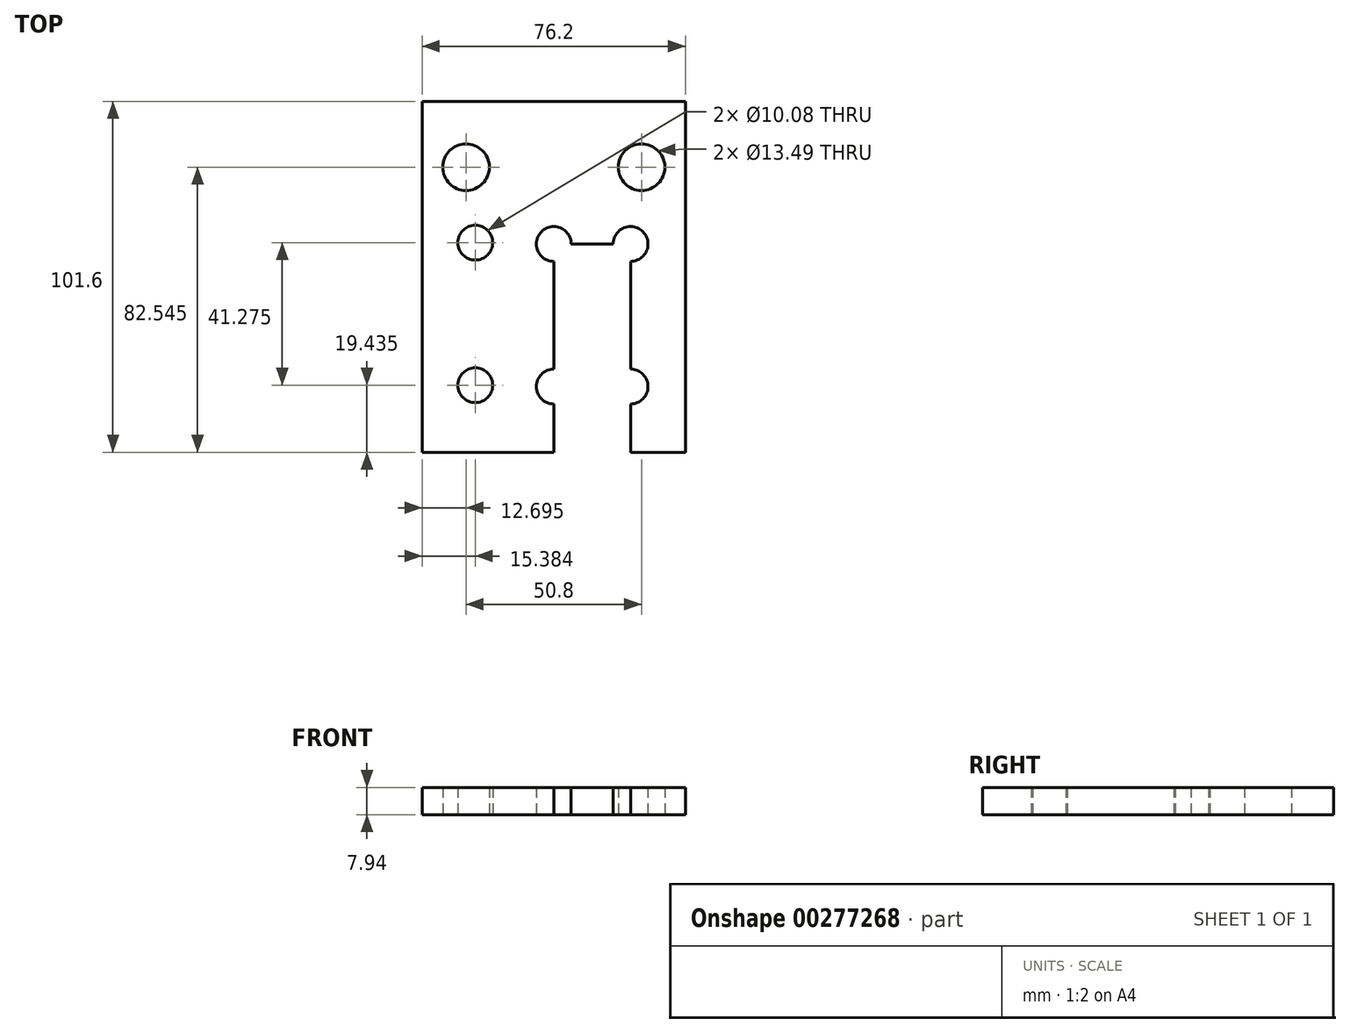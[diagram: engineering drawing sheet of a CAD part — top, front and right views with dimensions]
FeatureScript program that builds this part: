
annotation { "Feature Type Name" : "Feature", "Feature Type Description" : "" }
export const myFeature = defineFeature(function(context is Context, id is Id, definition is map)
    precondition{}
    {
        {
            var Q0;
            Q0=qCreatedBy(makeId("Top.planeOp"),FACE);
            var sketch = newSketch(context, id + "F0", { "sketchPlane" : qUnion([Q0])});
            skLineSegment(sketch, "E0.bottom", {"start": v(-37.95, 40.89) * mm, "end": v(38.25, 40.89) * mm});
            skLineSegment(sketch, "E0.top", {"start": v(-37.95, -60.71) * mm, "end": v(38.25, -60.71) * mm});
            skLineSegment(sketch, "E0.left", {"start": v(-37.95, 40.89) * mm, "end": v(-37.95, -60.71) * mm});
            skLineSegment(sketch, "E0.right", {"start": v(38.25, 40.89) * mm, "end": v(38.25, -60.71) * mm});
            skPoint(sketch, "E1", {"position": v(38.25, 40.89) * mm});
            skLineSegment(sketch, "E2", {"start": v(-25.25, 21.84) * mm, "end": v(-25.25, 40.89) * mm});
            skLineSegment(sketch, "E3", {"start": v(25.55, 21.84) * mm, "end": v(25.55, 40.89) * mm});
            skLineSegment(sketch, "E4", {"start": v(-25.25, 21.84) * mm, "end": v(-37.95, 21.84) * mm});
            skLineSegment(sketch, "E5", {"start": v(25.55, 21.84) * mm, "end": v(38.25, 21.84) * mm});
            skLineSegment(sketch, "E6", {"start": v(0.15, -0.39) * mm, "end": v(0.15, -41.66) * mm});
            skLineSegment(sketch, "E7", {"start": v(0.15, -41.66) * mm, "end": v(0.15, -60.71) * mm});
            skLineSegment(sketch, "E8", {"start": v(22.37, -0.39) * mm, "end": v(22.37, -41.66) * mm});
            skLineSegment(sketch, "E9", {"start": v(22.37, -41.66) * mm, "end": v(22.37, -60.71) * mm});
            skLineSegment(sketch, "E10", {"start": v(0.15, -0.39) * mm, "end": v(22.37, -0.39) * mm});
            skLineSegment(sketch, "E11", {"start": v(-22.57, 0) * mm, "end": v(-22.57, -41.28) * mm});
            skLineSegment(sketch, "E12", {"start": v(-22.57, -41.28) * mm, "end": v(-22.57, -60.33) * mm});
            skLineSegment(sketch, "E13", {"start": v(-22.57, 0) * mm, "end": v(-0.34, 0) * mm});
            skSolve(sketch);
        }
        {
            var Q0;
            {var subQ0=sQuery(id+"F0.wireOp",EDGE,"lcWCMHyC-eplE-XHto-Is1u-1jWQCE3xKe38");Q0=makeQuery(id+"F0.imprint","IMPRINT",FACE,{"disambiguationData":[TD([[makeQuery(id+"F0.imprint","IMPRINT",EDGE,{"derivedFrom":subQ0}),-1.0]])]});}
            var Q1;
            {var subQ0=sQuery(id+"F0.wireOp",EDGE,"PR7J1r9g-NyIZ-4EAv-97Ck-6R3T5vIXL9lI");Q1=makeQuery(id+"F0.imprint","IMPRINT",FACE,{"disambiguationData":[TD([[makeQuery(id+"F0.imprint","IMPRINT",EDGE,{"derivedFrom":subQ0}),-1.0]])]});}
            var Q2;
            {var subQ5=sQuery(id+"F0.wireOp",EDGE,"E0.top");Q2=makeQuery(id+"F0.imprint","IMPRINT",FACE,{"disambiguationData":[TD([[makeQuery(id+"F0.imprint","IMPRINT",EDGE,{"derivedFrom":subQ5}),1.0]])]});}
            var Q3;
            {var subQ3=sQuery(id+"F0.wireOp",EDGE,"0CVaf1VI-ZbOA-vU7j-4cAE-WN4LLiThvYsT");var subQ5=sQuery(id+"F0.wireOp",EDGE,"E0.left");var subQ6=makeQuery(id+"F0.imprint","INTERSECT",VERTEX,{"derivedFrom":[subQ3,subQ5]});Q3=makeQuery(id+"F0.imprint","IMPRINT",FACE,{"disambiguationData":[TD([[makeQuery(id+"F0.imprint","IMPRINT",EDGE,{"disambiguationData":[TD([[subQ6,-1.0]])],"derivedFrom":subQ3}),1.0]])]});}
            var Q4;
            {var subQ0=sQuery(id+"F0.wireOp",EDGE,"E2");var subQ1=sQuery(id+"F0.wireOp",EDGE,"LTa7V2wM-ZibM-cuZf-cZ65-yHtlyJLLMwwq");var subQ2=makeQuery(id+"F0.imprint","INTERSECT",VERTEX,{"derivedFrom":[subQ1,subQ0]});Q4=makeQuery(id+"F0.imprint","IMPRINT",FACE,{"disambiguationData":[TD([[makeQuery(id+"F0.imprint","IMPRINT",EDGE,{"disambiguationData":[TD([[subQ2,-1.0]])],"derivedFrom":subQ1}),-1.0]])]});}
            var Q5;
            {var subQ0=sQuery(id+"F0.wireOp",EDGE,"E3");var subQ1=sQuery(id+"F0.wireOp",EDGE,"ef0b0393-9919-4fb4-960b-99aeebce1d35");var subQ2=makeQuery(id+"F0.imprint","INTERSECT",VERTEX,{"derivedFrom":[subQ1,subQ0]});Q5=makeQuery(id+"F0.imprint","IMPRINT",FACE,{"disambiguationData":[TD([[makeQuery(id+"F0.imprint","IMPRINT",EDGE,{"disambiguationData":[TD([[subQ2,1.0]])],"derivedFrom":subQ1}),-1.0]])]});}
            var Q6;
            {var subQ0=sQuery(id+"F0.wireOp",EDGE,"leSzz3VN-8iKC-pAnP-wKXI-R4EXnybGQ6SQ");Q6=makeQuery(id+"F0.imprint","IMPRINT",FACE,{"disambiguationData":[TD([[makeQuery(id+"F0.imprint","IMPRINT",EDGE,{"derivedFrom":subQ0}),-1.0]])]});}
            var Q7;
            {var subQ0=sQuery(id+"F0.wireOp",EDGE,"sYbMa3EQ-lgzP-OEaw-l84T-zbEHqADuA0Jr");Q7=makeQuery(id+"F0.imprint","IMPRINT",FACE,{"disambiguationData":[TD([[makeQuery(id+"F0.imprint","IMPRINT",EDGE,{"derivedFrom":subQ0}),-1.0]])]});}
            var Q8;
            {var subQ7=sQuery(id+"F0.wireOp",EDGE,"2inGmozC-EzYw-nWrg-dNEA-qCZoMKFbgd93");Q8=makeQuery(id+"F0.imprint","IMPRINT",FACE,{"disambiguationData":[TD([[makeQuery(id+"F0.imprint","IMPRINT",EDGE,{"derivedFrom":subQ7}),-1.0]])]});}
            var Q9;
            {var subQ3=sQuery(id+"F0.wireOp",EDGE,"E2");Q9=makeQuery(id+"F0.imprint","IMPRINT",FACE,{"disambiguationData":[TD([[makeQuery(id+"F0.imprint","IMPRINT",EDGE,{"derivedFrom":subQ3}),1.0]])]});}
            var Q10;
            {var subQ3=sQuery(id+"F0.wireOp",EDGE,"E3");Q10=makeQuery(id+"F0.imprint","IMPRINT",FACE,{"disambiguationData":[TD([[makeQuery(id+"F0.imprint","IMPRINT",EDGE,{"derivedFrom":subQ3}),-1.0]])]});}
            var Q11;
            Q11=makeQuery(id+"F0.imprint","IMPRINT",FACE,{"disambiguationData":[TD([[makeQuery(id+"F0.imprint","IMPRINT",EDGE,{"derivedFrom":sQuery(id+"F0.wireOp",EDGE,"E6")}),-1.0]])]});
            extrude(context, id + "F1", {"entities" : qUnion([Q0, Q1, Q2, Q3, Q4, Q5, Q6, Q7, Q8, Q9, Q10, Q11]), "depth" : 7.94 * mm});
        }
        {
            var Q0;
            Q0=sQuery(id+"F0.wireOp",VERTEX,"slWlOJYp-KtXo-T63F-XDAo-gwFZsbOWbfFg.start");
            var Q1;
            Q1=sQuery(id+"F0.wireOp",VERTEX,"2inGmozC-EzYw-nWrg-dNEA-qCZoMKFbgd93.start");
            var Q2;
            Q2=sQuery(id+"F0.wireOp",VERTEX,"E6.start");
            var Q3;
            Q3=sQuery(id+"F0.wireOp",VERTEX,"E7.start");
            var Q4;
            Q4=sQuery(id+"F0.wireOp",VERTEX,"f259f9f2-1a3e-449f-ba45-59925c1e67a2.start");
            var Q5;
            Q5=sQuery(id+"F0.wireOp",VERTEX,"06f6825e-fbd1-4fb1-a750-9c05bcffc3f1.start");
            var Q6;
            Q6=sQuery(id+"F0.wireOp",VERTEX,"E11.start");
            var Q7;
            Q7=sQuery(id+"F0.wireOp",VERTEX,"E12.start");
            var Q8;
            Q8=sQuery(id+"F0.wireOp",VERTEX,"E9.start");
            var Q9;
            Q9=sQuery(id+"F0.wireOp",VERTEX,"E8.start");
            var Q10;
            Q10=makeQuery(id+"F1.opExtrude","SWEPT_BODY",BODY,{"disambiguationData":[OSD([sQuery(id+"F0.wireOp",EDGE,"MnHyicGj-JLrE-Ki9W-tNHr-ggfPMjACvSpb.bottom"),sQuery(id+"F0.wireOp",EDGE,"PR7J1r9g-NyIZ-4EAv-97Ck-6R3T5vIXL9lI"),sQuery(id+"F0.wireOp",EDGE,"sYbMa3EQ-lgzP-OEaw-l84T-zbEHqADuA0Jr"),sQuery(id+"F0.wireOp",EDGE,"E0.bottom"),sQuery(id+"F0.wireOp",EDGE,"E0.top"),sQuery(id+"F0.wireOp",EDGE,"lcWCMHyC-eplE-XHto-Is1u-1jWQCE3xKe38"),sQuery(id+"F0.wireOp",EDGE,"leSzz3VN-8iKC-pAnP-wKXI-R4EXnybGQ6SQ"),sQuery(id+"F0.wireOp",EDGE,"LTa7V2wM-ZibM-cuZf-cZ65-yHtlyJLLMwwq"),sQuery(id+"F0.wireOp",EDGE,"ef0b0393-9919-4fb4-960b-99aeebce1d35"),sQuery(id+"F0.wireOp",EDGE,"y1FCQ7DP-OZn0-aLE5-Vu3G-GsuLOWiZEw8X"),sQuery(id+"F0.wireOp",EDGE,"pVYJsK03-gGuF-Nf4y-ptFC-W02t8f7CweEY")])]});
            hole(context, id + "F2", {"style" : HoleStyle.SIMPLE, "endStyle" : HoleEndStyle.THROUGH, "oppositeDirection" : true, "standardTappedOrClearance" : lookupTablePath({ "standard" : "ANSI", "fit" : "Normal (ASME)", "size" : "3/8", "type" : "Clearance" }), "standardBlindInLast" : lookupTablePath({ "fit" : "Free", "standard" : "ANSI", "size" : "3/8", "type" : "Clearance" }), "holeDiameter" : 10.08 * mm, "tappedDepth" : 12.7 * mm, "tapClearance" : 3, "locations" : qUnion([Q0, Q1, Q2, Q3, Q4, Q5, Q6, Q7, Q8, Q9]), "scope" : qUnion([Q10])});
        }
        {
            var Q0;
            Q0=sQuery(id+"F0.wireOp",VERTEX,"E2.start");
            var Q1;
            Q1=sQuery(id+"F0.wireOp",VERTEX,"E5.start");
            var Q2;
            Q2=makeQuery(id+"F1.opExtrude","SWEPT_BODY",BODY,{"disambiguationData":[OSD([sQuery(id+"F0.wireOp",EDGE,"MnHyicGj-JLrE-Ki9W-tNHr-ggfPMjACvSpb.bottom"),sQuery(id+"F0.wireOp",EDGE,"PR7J1r9g-NyIZ-4EAv-97Ck-6R3T5vIXL9lI"),sQuery(id+"F0.wireOp",EDGE,"sYbMa3EQ-lgzP-OEaw-l84T-zbEHqADuA0Jr"),sQuery(id+"F0.wireOp",EDGE,"E0.bottom"),sQuery(id+"F0.wireOp",EDGE,"E0.top"),sQuery(id+"F0.wireOp",EDGE,"lcWCMHyC-eplE-XHto-Is1u-1jWQCE3xKe38"),sQuery(id+"F0.wireOp",EDGE,"leSzz3VN-8iKC-pAnP-wKXI-R4EXnybGQ6SQ"),sQuery(id+"F0.wireOp",EDGE,"y1FCQ7DP-OZn0-aLE5-Vu3G-GsuLOWiZEw8X"),sQuery(id+"F0.wireOp",EDGE,"pVYJsK03-gGuF-Nf4y-ptFC-W02t8f7CweEY")])]});
            hole(context, id + "F3", {"style" : HoleStyle.SIMPLE, "endStyle" : HoleEndStyle.THROUGH, "oppositeDirection" : true, "standardTappedOrClearance" : lookupTablePath({ "standard" : "ANSI", "fit" : "Normal (ASME)", "size" : "1/2", "type" : "Clearance" }), "standardBlindInLast" : lookupTablePath({ "fit" : "Free", "standard" : "ANSI", "size" : "1/2", "type" : "Clearance" }), "holeDiameter" : 13.5 * mm, "tappedDepth" : 12.7 * mm, "tapClearance" : 3, "locations" : qUnion([Q0, Q1]), "scope" : qUnion([Q2])});
        }
    });
